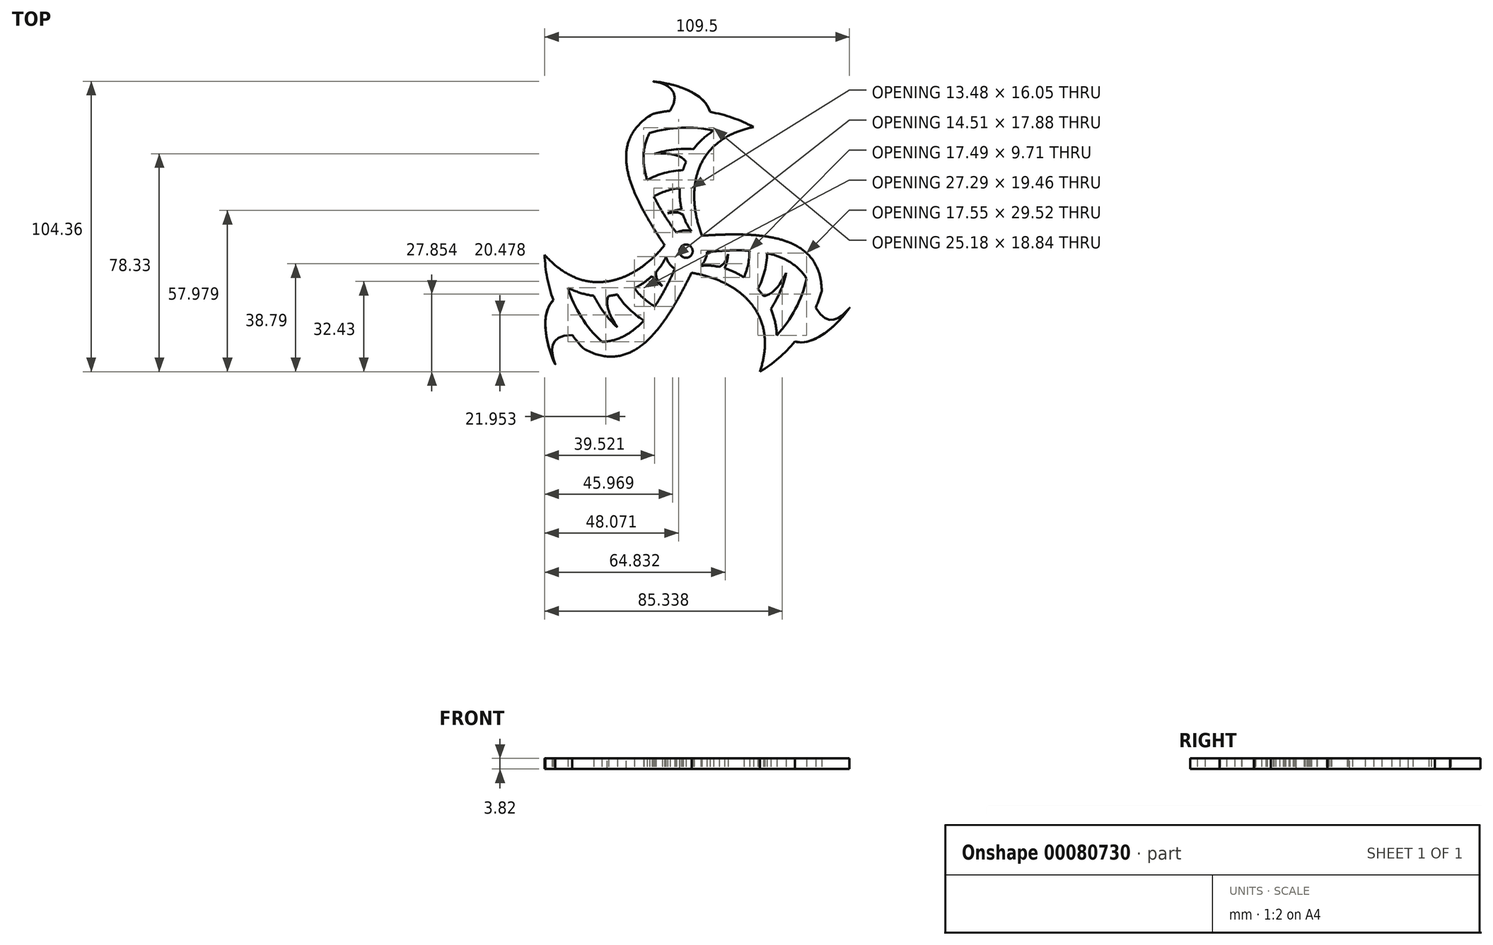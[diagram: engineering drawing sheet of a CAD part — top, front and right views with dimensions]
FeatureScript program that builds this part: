
annotation { "Feature Type Name" : "Feature", "Feature Type Description" : "" }
export const myFeature = defineFeature(function(context is Context, id is Id, definition is map)
    precondition{}
    {
        {
            var Q0;
            Q0=qCreatedBy(makeId("Top.planeOp"),FACE);
            var sketch = newSketch(context, id + "F0", { "sketchPlane" : qUnion([Q0])});
            skCircle(sketch, "E0", {"center": v(0, 0) * mm, "radius": 50.8 * mm});
            skCircle(sketch, "E1", {"center": v(0, 0) * mm, "radius": 2.37 * mm});
            skCircle(sketch, "E2", {"center": v(0, 0) * mm, "radius": 7.5 * mm});
            skFitSpline(sketch, "E3", {"points": [v(-7.33, 1.58) * mm, v(-11.96, 49.37) * mm], "startDerivative": vector(-34.7, 51.98) * mm, "endDerivative": vector(54.42, 32.42) * mm});
            skFitSpline(sketch, "E4", {"points": [v(6.8, 3.16) * mm, v(24.25, 44.64) * mm], "startDerivative": vector(-20.38, 43.44) * mm, "endDerivative": vector(72.54, 15) * mm});
            skFitSpline(sketch, "E5", {"points": [v(8.6, 50.07) * mm, v(-11.7, 61.01) * mm, v(-5.7, 50.48) * mm], "startDerivative": vector(-14.05, 50.07) * mm, "endDerivative": vector(-40.72, -66.06) * mm});
            skCircle(sketch, "E6", {"center": v(0, 0) * mm, "radius": 44.45 * mm});
            skFitSpline(sketch, "E7", {"points": [v(-3.48, 6.63) * mm, v(-5.7, 50.48) * mm], "startDerivative": vector(-30.89, 42.81) * mm, "endDerivative": vector(51.45, 37.06) * mm});
            skFitSpline(sketch, "E8", {"points": [v(1.93, 7.24) * mm, v(18.5, 47.31) * mm], "startDerivative": vector(-19.74, 24.24) * mm, "endDerivative": vector(74.82, 23.94) * mm});
            skCircle(sketch, "E9", {"center": v(0, 0) * mm, "radius": 29.15 * mm});
            skCircle(sketch, "E10", {"center": v(0, 0) * mm, "radius": 22.8 * mm});
            skLineSegment(sketch, "E11", {"start": v(-44.45, 0) * mm, "end": v(-29.15, 0) * mm, "construction": true});
            skLineSegment(sketch, "E12", {"start": v(-22.8, 0) * mm, "end": v(-7.5, 0) * mm, "construction": true});
            skLineSegment(sketch, "E13", {"start": v(22.8, 0) * mm, "end": v(29.15, 0) * mm, "construction": true});
            skLineSegment(sketch, "E14", {"start": v(44.45, 0) * mm, "end": v(50.8, 0) * mm, "construction": true});
            skCircle(sketch, "E15", {"center": v(0, 0) * mm, "radius": 36.8 * mm});
            skLineSegment(sketch, "E16", {"start": v(29.15, 0) * mm, "end": v(36.8, 0) * mm, "construction": true});
            skLineSegment(sketch, "E17", {"start": v(36.8, 0) * mm, "end": v(44.45, 0) * mm, "construction": true});
            skFitSpline(sketch, "E18", {"points": [v(0, 32.1) * mm, v(-11.28, 35.03) * mm], "startDerivative": vector(-3.5, 5.56) * mm, "endDerivative": vector(-20.7, -1.7) * mm});
            skCircle(sketch, "E19", {"center": v(0, 0) * mm, "radius": 15.14 * mm});
            skLineSegment(sketch, "E20", {"start": v(7.5, 0) * mm, "end": v(15.14, 0) * mm, "construction": true});
            skLineSegment(sketch, "E21", {"start": v(15.14, 0) * mm, "end": v(22.8, 0) * mm, "construction": true});
            skFitSpline(sketch, "E22", {"points": [v(-1.08, 13.13) * mm, v(-6.62, 13.62) * mm], "startDerivative": vector(-5.42, 2.86) * mm, "endDerivative": vector(-10.03, -1.88) * mm});
            skSolve(sketch);
        }
        {
            var Q0;
            {var subQ0=sQuery(id+"F0.wireOp",EDGE,"E3");Q0=makeQuery(id+"F0.imprint","IMPRINT",FACE,{"disambiguationData":[TD([[makeQuery(id+"F0.imprint","IMPRINT",EDGE,{"derivedFrom":subQ0}),-1.0]])]});}
            var Q1;
            Q1=makeQuery(id+"F0.imprint","IMPRINT",FACE,{"disambiguationData":[TD([[makeQuery(id+"F0.imprint","IMPRINT",EDGE,{"derivedFrom":sQuery(id+"F0.wireOp",EDGE,"E1")}),-1.0]])]});
            var Q2;
            {var subQ0=sQuery(id+"F0.wireOp",EDGE,"E5");Q2=makeQuery(id+"F0.imprint","IMPRINT",FACE,{"disambiguationData":[TD([[makeQuery(id+"F0.imprint","IMPRINT",EDGE,{"derivedFrom":subQ0}),1.0]])]});}
            var Q3;
            {var subQ1=sQuery(id+"F0.wireOp",EDGE,"E5");var subQ2=sQuery(id+"F0.wireOp",EDGE,"E0");var subQ6=makeQuery(id+"F0.imprint","INTERSECT",VERTEX,{"derivedFrom":[subQ2,subQ1]});Q3=makeQuery(id+"F0.imprint","IMPRINT",FACE,{"disambiguationData":[TD([[makeQuery(id+"F0.imprint","IMPRINT",EDGE,{"disambiguationData":[TD([[subQ6,1.0]])],"derivedFrom":subQ2}),1.0]])]});}
            var Q4;
            {var subQ0=sQuery(id+"F0.wireOp",EDGE,"E4");var subQ1=sQuery(id+"F0.wireOp",EDGE,"E0");var subQ2=makeQuery(id+"F0.imprint","INTERSECT",VERTEX,{"derivedFrom":[subQ1,subQ0]});Q4=makeQuery(id+"F0.imprint","IMPRINT",FACE,{"disambiguationData":[TD([[makeQuery(id+"F0.imprint","IMPRINT",EDGE,{"disambiguationData":[TD([[subQ2,-1.0]])],"derivedFrom":subQ1}),1.0]])]});}
            var Q5;
            {var subQ0=sQuery(id+"F0.wireOp",EDGE,"E9");var subQ1=sQuery(id+"F0.wireOp",EDGE,"E4");var subQ2=makeQuery(id+"F0.imprint","INTERSECT",VERTEX,{"derivedFrom":[subQ1,subQ0]});Q5=makeQuery(id+"F0.imprint","IMPRINT",FACE,{"disambiguationData":[TD([[makeQuery(id+"F0.imprint","IMPRINT",EDGE,{"disambiguationData":[TD([[subQ2,-1.0]])],"derivedFrom":subQ1}),1.0]])]});}
            var Q6;
            {var subQ0=sQuery(id+"F0.wireOp",EDGE,"E10");var subQ1=sQuery(id+"F0.wireOp",EDGE,"E4");var subQ2=makeQuery(id+"F0.imprint","INTERSECT",VERTEX,{"derivedFrom":[subQ1,subQ0]});Q6=makeQuery(id+"F0.imprint","IMPRINT",FACE,{"disambiguationData":[TD([[makeQuery(id+"F0.imprint","IMPRINT",EDGE,{"disambiguationData":[TD([[subQ2,-1.0]])],"derivedFrom":subQ1}),1.0]])]});}
            var Q7;
            {var subQ0=sQuery(id+"F0.wireOp",EDGE,"E8");var subQ1=sQuery(id+"F0.wireOp",EDGE,"E2");var subQ2=makeQuery(id+"F0.imprint","INTERSECT",VERTEX,{"derivedFrom":[subQ1,subQ0]});Q7=makeQuery(id+"F0.imprint","IMPRINT",FACE,{"disambiguationData":[TD([[makeQuery(id+"F0.imprint","IMPRINT",EDGE,{"disambiguationData":[TD([[subQ2,1.0]])],"derivedFrom":subQ1}),-1.0]])]});}
            var Q8;
            {var subQ0=sQuery(id+"F0.wireOp",EDGE,"E10");var subQ1=sQuery(id+"F0.wireOp",EDGE,"E7");var subQ2=makeQuery(id+"F0.imprint","INTERSECT",VERTEX,{"derivedFrom":[subQ1,subQ0]});Q8=makeQuery(id+"F0.imprint","IMPRINT",FACE,{"disambiguationData":[TD([[makeQuery(id+"F0.imprint","IMPRINT",EDGE,{"disambiguationData":[TD([[subQ2,-1.0]])],"derivedFrom":subQ1}),-1.0]])]});}
            var Q9;
            {var subQ0=sQuery(id+"F0.wireOp",EDGE,"E9");var subQ1=sQuery(id+"F0.wireOp",EDGE,"E3");var subQ2=makeQuery(id+"F0.imprint","INTERSECT",VERTEX,{"derivedFrom":[subQ1,subQ0]});Q9=makeQuery(id+"F0.imprint","IMPRINT",FACE,{"disambiguationData":[TD([[makeQuery(id+"F0.imprint","IMPRINT",EDGE,{"disambiguationData":[TD([[subQ2,-1.0]])],"derivedFrom":subQ1}),-1.0]])]});}
            var Q10;
            {var subQ0=sQuery(id+"F0.wireOp",EDGE,"02ee5eb9-fec3-4d49-90e1-4be1db1b977d");Q10=makeQuery(id+"F0.imprint","IMPRINT",FACE,{"disambiguationData":[TD([[makeQuery(id+"F0.imprint","IMPRINT",EDGE,{"derivedFrom":subQ0}),1.0]])]});}
            var Q11;
            {var subQ0=sQuery(id+"F0.wireOp",EDGE,"E15");var subQ1=sQuery(id+"F0.wireOp",EDGE,"E4");var subQ2=makeQuery(id+"F0.imprint","INTERSECT",VERTEX,{"derivedFrom":[subQ1,subQ0]});Q11=makeQuery(id+"F0.imprint","IMPRINT",FACE,{"disambiguationData":[TD([[makeQuery(id+"F0.imprint","IMPRINT",EDGE,{"disambiguationData":[TD([[subQ2,-1.0]])],"derivedFrom":subQ1}),1.0]])]});}
            var Q12;
            {var subQ0=sQuery(id+"F0.wireOp",EDGE,"E18");Q12=makeQuery(id+"F0.imprint","IMPRINT",FACE,{"disambiguationData":[TD([[makeQuery(id+"F0.imprint","IMPRINT",EDGE,{"derivedFrom":subQ0}),-1.0]])]});}
            var Q13;
            {var subQ4=sQuery(id+"F0.wireOp",EDGE,"E2");var subQ6=sQuery(id+"F0.wireOp",EDGE,"E3");var subQ7=makeQuery(id+"F0.imprint","INTERSECT",VERTEX,{"derivedFrom":[subQ4,subQ6]});Q13=makeQuery(id+"F0.imprint","IMPRINT",FACE,{"disambiguationData":[TD([[makeQuery(id+"F0.imprint","IMPRINT",EDGE,{"disambiguationData":[TD([[subQ7,1.0]])],"derivedFrom":subQ4}),-1.0]])]});}
            var Q14;
            {var subQ0=sQuery(id+"F0.wireOp",EDGE,"b8c473f6-a033-4eba-b6a9-50cacf2a13a1");Q14=makeQuery(id+"F0.imprint","IMPRINT",FACE,{"disambiguationData":[TD([[makeQuery(id+"F0.imprint","IMPRINT",EDGE,{"derivedFrom":subQ0}),1.0]])]});}
            var Q15;
            {var subQ0=sQuery(id+"F0.wireOp",EDGE,"E19");var subQ1=sQuery(id+"F0.wireOp",EDGE,"E4");var subQ2=makeQuery(id+"F0.imprint","INTERSECT",VERTEX,{"derivedFrom":[subQ1,subQ0]});Q15=makeQuery(id+"F0.imprint","IMPRINT",FACE,{"disambiguationData":[TD([[makeQuery(id+"F0.imprint","IMPRINT",EDGE,{"disambiguationData":[TD([[subQ2,-1.0]])],"derivedFrom":subQ1}),1.0]])]});}
            var Q16;
            {var subQ0=sQuery(id+"F0.wireOp",EDGE,"E22");Q16=makeQuery(id+"F0.imprint","IMPRINT",FACE,{"disambiguationData":[TD([[makeQuery(id+"F0.imprint","IMPRINT",EDGE,{"derivedFrom":subQ0}),-1.0]])]});}
            extrude(context, id + "F1", {"entities" : qUnion([Q0, Q1, Q2, Q3, Q4, Q5, Q6, Q7, Q8, Q9, Q10, Q11, Q12, Q13, Q14, Q15, Q16]), "endBound" : BoundingType.SYMMETRIC, "depth" : 3.8 * mm});
        }
        {
            var Q0;
            Q0=makeQuery(id+"F1.opExtrude","SWEPT_BODY",BODY,{"disambiguationData":[OSD([sQuery(id+"F0.wireOp",EDGE,"E0"),sQuery(id+"F0.wireOp",EDGE,"E1"),sQuery(id+"F0.wireOp",EDGE,"E2"),sQuery(id+"F0.wireOp",EDGE,"E3"),sQuery(id+"F0.wireOp",EDGE,"E4"),sQuery(id+"F0.wireOp",EDGE,"E5")])]});
            var Q1;
            Q1=makeQuery(id+"F1.opExtrude","CAP_EDGE",EDGE,{"disambiguationData":[OSD([sQuery(id+"F0.wireOp",EDGE,"E1")])],"isStart":false});
            circularPattern(context, id + "F2", {"operationType" : NewBodyOperationType.ADD, "entities" : qUnion([Q0]), "axis" : qUnion([Q1]), "angle" : 360 * degree, "instanceCount" : 3, "equalSpace" : true});
        }
        {
            var Q0;
            Q0=makeQuery(id+"F1.opExtrude","SWEPT_EDGE",EDGE,{"disambiguationData":[OSD([sQuery(id+"F0.wireOp",EDGE,"E0"),sQuery(id+"F0.wireOp",EDGE,"E3")])]});
            var Q1;
            Q1=makeQuery(id+"F2.opPattern","COPY",EDGE,{"derivedFrom":makeQuery(id+"F1.opExtrude","SWEPT_EDGE",EDGE,{"disambiguationData":[OSD([sQuery(id+"F0.wireOp",EDGE,"E0"),sQuery(id+"F0.wireOp",EDGE,"E3")])]}),"instanceName":"1"});
            fillet(context, id + "F3", {"entities" : qUnion([Q0, Q1]), "radius" : 5.08 * mm, "tangentPropagation" : true, "allowEdgeOverflow" : false});
        }
    });
